# Revit family: FP-Revit18-en-DD24DTX6I1-DD24DTX6HI1-DishDrawer-0-90001208B-US-CA
name_source: partatom
category: Specialty Equipment
units: mm (PartAtom-declared; Revit-internal decimal feet)

## family parameters
Always vertical = Yes
Cut with Voids When Loaded = Yes
OmniClass Number = 23.40.40.14.31
OmniClass Title = Cleaning and Disposal Equipment
Part Type = Normal
Room Calculation Point = No
Round Connector Dimension = Use Diameter
Shared = No
Work Plane-Based = No

## types (2) — shared parameters
Cavity - Depth (excluding front panel) = 560 mm  [stored 1.83727 ft]
Cavity - Width = 600 mm  [stored 1.9685 ft]
Chassis - Depth = 553 mm  [stored 1.8143 ft]
Chassis - Height (855mm Tall or 811mm Std) = 855 mm  [stored 2.80512 ft]
Connector Description - Water = 3/4” BSP (GB20) to suit flat washer
Description = 60cm DishDrawer, Integrated
Lower panel extension (311 - 361mm) = 311 mm  [stored 1.02034 ft]
Manufacturer = Fisher & Paykel Appliances
Material - Body = Fisher & Paykel - Grey
Material - Front = Fisher & Paykel - Stainless Steel
Material - Toe Kick = Fisher & Paykel - Stainless Steel
Material - Trim = Fisher & Paykel - Black
Product - Depth = 571 mm  [stored 1.87336 ft]
Product - Width = 599 mm  [stored 1.96522 ft]
Toe Kick - Recess (40mm - 100mm) = 100 mm  [stored 0.328084 ft]
URL = www.fisherpaykel.com
Visibility - Clearance Required = Yes
zero-valued in all types: Default Elevation

## per-type parameters (varying)
| type | Connector Description - Electrical | Connector Description - Sanitary | Model | Product - Height (864mm - 924mm) | Visibility - Door Panel | Visibility - Toe Kick |
| DD24DTX6I1-DD24DTX6HI1 | 120V, 60 Hz, min 8.7 A, fused electrical supply | Drain Hose to spigot or standpipe | DD60DTX6HI1 | 924 mm  [stored 3.0315 ft] | Yes | Yes |
| DD60DTX6I1 | 220-240 V, 50 Hz, min 8.5 A, fused electrical supply | Drain Hose, No Fitting Required | DD60DTX6I1 | 900 mm  [stored 2.95276 ft] | No | No |

note: [stored X ft] marks values corroborated as IEEE doubles in the binary element streams (Revit-internal decimal feet)

## geometry (parser evidence)
native form markers: Sweep x2
no freeform markers — native parametric forms only
